# Revit family: CMAC_Blast Chillers_ST10--
name_source: partatom
category: Specialty Equipment
revit_build: Autodesk Revit 2016 (Build: 20150714_1515(x64)
units: mm (PartAtom-declared; Revit-internal decimal feet)

## family parameters
Always vertical = Yes
Cut with Voids When Loaded = No
OmniClass Number = 23.40.40.14.27
OmniClass Title = Ice Machines
Part Type = Normal
Room Calculation Point = No
Round Connector Dimension = Use Diameter
Shared = No
Work Plane-Based = No

## types (1)
- W800 D700 H1505 mm AIR
    Air Exchange Volume = 1000 m³
    Ambient Temperature MinMax = 10°C/32°C
    Assembly Code = E1090320
    Clearance W = 150 mm
    Cold Water DN = 0 mm
    Cold Water DN Type = -
    Cold Water Flow = 0.0 L/s
    Cold Water Pressure MinMax = 1bar/5bar
    Cold Water Temperature MinMax = 5°C/35°C
    Condensation Heat Expelled = 4650 W
    Condensation Type = AIR
    Cooling Capacity = 3 kW
    Depth = 700 mm  [stored 2.29659 ft]
    ELE_Frequency = 50 Hz
    ELE_Fuse = 16 A
    ELE_Number of poles = 1
    ELE_Power = 2 kW
    ELE_Power 1kg = 0 kWh
    ELE_Power Supply = 230 V
    Exhaust Condensate Water DN = 20 mm
    Exhaust Condensate Water DN Type = 20
    File Release = R001
    Fillet = 0 mm  [stored 0 ft]
    Height = 1505 mm  [stored 4.93766 ft]
    IFC Classification = Furnishing Element
    Keynote = ABB10ECO
    LOD Data = 400
    LOD Model = 400
    Manufacturer = Icematic - Castel MAC S.p.a.
    Mat Cabinet = ALI_Stainless Steel
    Mat Clearance = ALI_Clearance
    Mat Door = ALI_Plastic_Black_Low Gloss
    Mat Legs = ALI_Stainless Steel
    Model = ABB10ECO
    Product Code = CM969095A3/0
    Product Manufacturer = Icematic - Castel MAC S.p.a.
    Product Series = ABB10ECO
    Product URL = http://www.icematic.eu
    R12 = 12 mm  [stored 0.0393701 ft]
    Refrigerant Gas Charge = 2.20 kg
    Refrigerant Gas GWP = 2141
    Refrigerant Gas Ton CO2 eq = 4710.00 kg
    Refrigerant Gas Type = R452A
    URL = https://www.castelmac.eu
    Volume = 0.84 m³
    Weight net = 139.00 kg
    Width = 800 mm  [stored 2.62467 ft]

note: [stored X ft] marks values corroborated as IEEE doubles in the binary element streams (Revit-internal decimal feet)

## geometry (parser evidence)
native form markers: Sweep x10
no freeform markers — native parametric forms only
